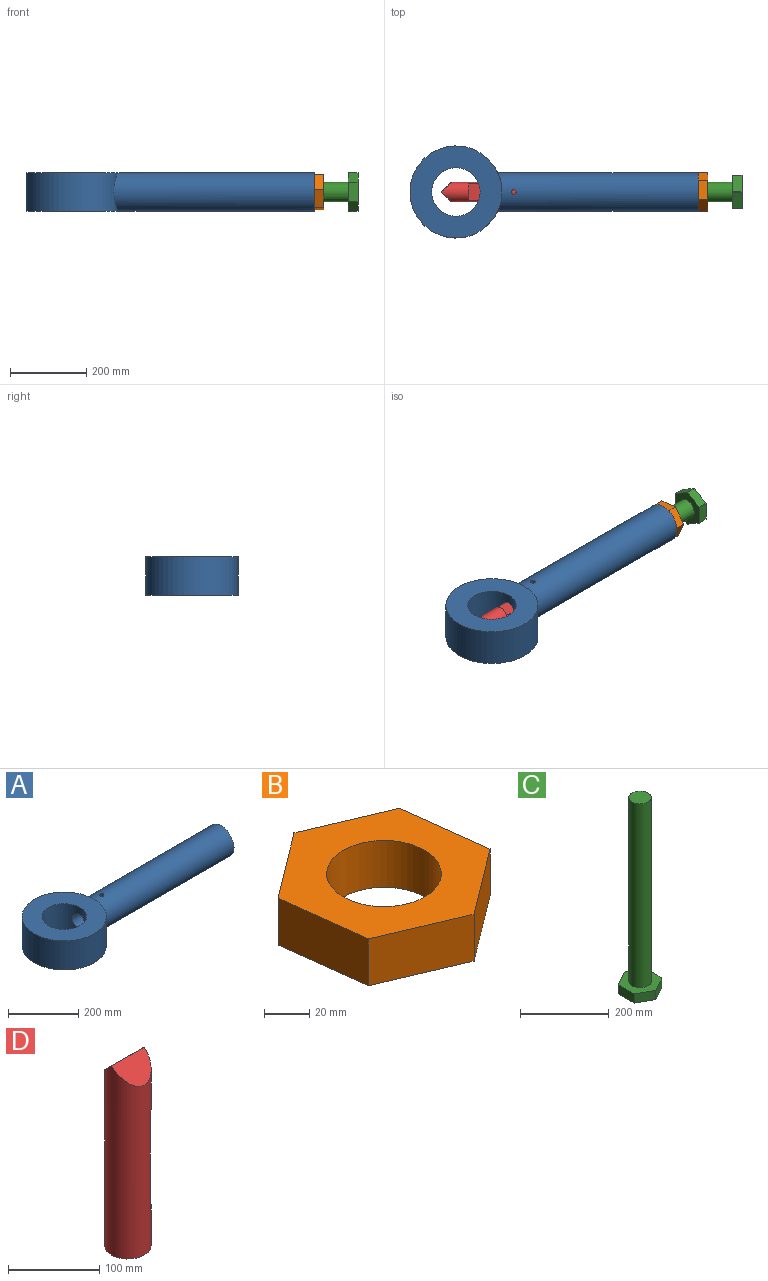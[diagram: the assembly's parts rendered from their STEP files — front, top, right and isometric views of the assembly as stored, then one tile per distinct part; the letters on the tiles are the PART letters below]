
ASSEMBLY  parts=4 mates=3
PART A: 8 faces, bbox 755.7x241.3x101.6 mm
  f0: cylinder r=120.65mm len=241.3mm, axis (0,0,-1), area 68718.9mm2, adj f3,f4,f6
  f1: plane 101.6x101.6mm, normal (1,0,0), area 6080.5mm2, adj f5,f6
  f2: cylinder r=63.5mm len=127mm, axis (0,0,-1), area 38466.5mm2, adj f3,f4,f5
  f3: plane 241.3x241.3mm, normal (0,0,-1), area 33062.7mm2, adj f0,f2
  f4: plane 241.3x241.3mm, normal (0,0,1), area 33062.7mm2, adj f0,f2
  f5: cylinder r=25.4mm len=576.8mm, axis (-1,0,0), area 91498mm2, adj f1,f2,f7
  f6: cylinder r=50.8mm len=525.57mm, axis (-1,0,0), area 165814.4mm2, adj f0,f1,f7
  f7: cylinder r=6.35mm len=26.21mm, axis (0,0,1), area 1021.5mm2, adj f5,f6
PART B: 9 faces, bbox 93.2x100.5x25.4 mm
  f0: plane 40.45x30.44mm, normal (0.6,-0.8,0), area 1285.8mm2, adj f1,f6,f7,f8
  f1: plane 50.25x25.4mm, normal (0.99,0.12,0), area 1285.8mm2, adj f0,f2,f7,f8
  f2: plane 46.59x25.4mm, normal (0.39,0.92,0), area 1285.8mm2, adj f1,f3,f7,f8
  f3: plane 40.45x30.44mm, normal (-0.6,0.8,0), area 1285.8mm2, adj f2,f4,f7,f8
  f4: plane 50.25x25.4mm, normal (-0.99,-0.12,0), area 1285.8mm2, adj f3,f6,f7,f8
  f5: cylinder r=25.4mm len=50.8mm, axis (0,0,-1), area 4053.7mm2, adj f7,f8
  f6: plane 46.59x25.4mm, normal (-0.39,-0.92,0), area 1285.8mm2, adj f0,f4,f7,f8
  f7: plane 100.5x93.17mm, normal (0,0,1), area 4631.3mm2, adj f0,f1,f2,f3,f4,f5,f6
  f8: plane 100.5x93.17mm, normal (0,0,-1), area 4631.3mm2, adj f0,f1,f2,f3,f4,f5,f6
PART C: 16 faces, bbox 88.2x101.6x533.4 mm
  f0: cylinder r=50.8mm len=25.4mm, axis (0,0,-1), area 9.4mm2, adj f1,f11,f12,f13
  f1: plane 50.48x25.4mm, normal (1,0,0), area 1282.2mm2, adj f0,f2,f12,f13
  f2: cylinder r=50.8mm len=25.4mm, axis (0,0,-1), area 9.4mm2, adj f1,f3,f12,f13
  f3: plane 43.72x25.4mm, normal (0.5,0.87,0), area 1282.2mm2, adj f2,f4,f12,f13
  f4: cylinder r=50.8mm len=25.4mm, axis (0,0,-1), area 9.4mm2, adj f3,f5,f12,f13
  f5: plane 43.72x25.4mm, normal (-0.5,0.87,0), area 1282.2mm2, adj f4,f6,f12,f13
  f6: cylinder r=50.8mm len=25.4mm, axis (0,0,-1), area 9.4mm2, adj f5,f7,f12,f13
  f7: plane 50.48x25.4mm, normal (-1,0,0), area 1282.2mm2, adj f6,f8,f12,f13
  f8: cylinder r=50.8mm len=25.4mm, axis (0,0,-1), area 9.4mm2, adj f7,f9,f12,f13
  f9: plane 43.72x25.4mm, normal (-0.5,-0.87,0), area 1282.2mm2, adj f8,f10,f12,f13
  f10: cylinder r=50.8mm len=25.4mm, axis (0,0,-1), area 9.4mm2, adj f9,f11,f12,f13
  f11: plane 43.72x25.4mm, normal (0.5,-0.87,0), area 1282.2mm2, adj f0,f10,f12,f13
  f12: plane 101.6x88.17mm, normal (0,0,1), area 4705.8mm2, adj f0,f1,f2,f3,f4,f5,f6,f7
  f13: plane 101.6x88.17mm, normal (0,0,-1), area 6732.6mm2, adj f0,f1,f2,f3,f4,f5,f6,f7
  f14: cylinder r=25.4mm len=508mm, axis (0,0,-1), area 81073.2mm2, adj f12,f15
  f15: plane 50.8x50.8mm, normal (0,0,1), area 2026.8mm2, adj f14
PART D: 7 faces, bbox 50.8x50.8x254 mm
  f0: plane 50.8x25.4mm, normal (0,-0.71,0.71), area 1433.2mm2, adj f4,f5
  f1: plane 43.99x12.7mm, normal (0,0,1), area 396.2mm2, adj f3,f5
  f2: plane 43.99x12.7mm, normal (0,0,-1), area 396.2mm2, adj f3,f5
  f3: plane 129.31x43.99mm, normal (1,0,0), area 5688.7mm2, adj f1,f2,f5
  f4: plane 50.8x25.4mm, normal (0,0.71,0.71), area 1433.2mm2, adj f0,f5
  f5: cylinder r=25.4mm len=254mm, axis (0,0,-1), area 31077.2mm2, adj f0,f1,f2,f3,f4,f6
  f6: plane 50.8x50.8mm, normal (0,0,-1), area 2026.8mm2, adj f5
PLACE A t=(0,58.67,-10.01)mm
PLACE B rot(axis=(0.71,0,-0.71),180deg) t=(660.4,-259.79,308.84)mm
PLACE C rot(axis=(0.58,-0.58,-0.58),120deg) t=(749.74,-239.71,32.19)mm
PLACE D rot(axis=(0,-1,0),90deg) t=(343.34,-161.36,-224.61)mm
MATE revolute D.f5 <-> C.f0  axis (1,0,0) through (216.34,58.67,40.79)mm
MATE fastened B.f5 <-> A.f5  axis (-1,0,0) through (635,58.67,40.79)mm
MATE cylindrical C.f0 <-> B.f5  axis (1,0,0) through (470.34,58.67,40.79)mm
